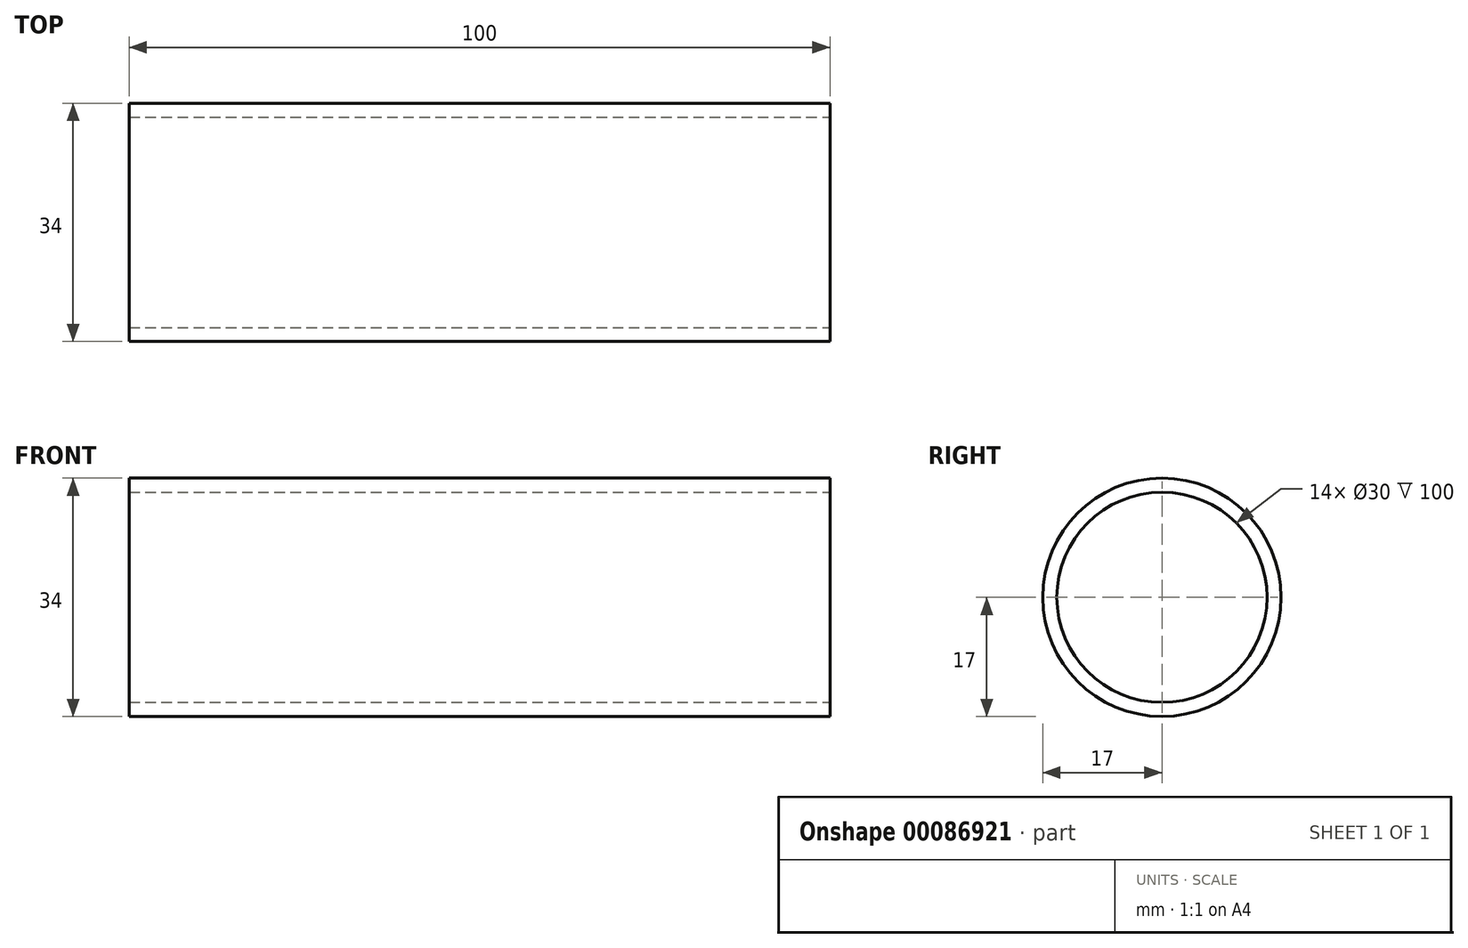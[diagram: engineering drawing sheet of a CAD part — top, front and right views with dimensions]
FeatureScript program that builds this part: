
annotation { "Feature Type Name" : "Feature", "Feature Type Description" : "" }
export const myFeature = defineFeature(function(context is Context, id is Id, definition is map)
    precondition{}
    {
        {
            var Q0;
            Q0=qCreatedBy(makeId("Top.planeOp"),FACE);
            var sketch = newSketch(context, id + "F0", { "sketchPlane" : qUnion([Q0])});
            skLineSegment(sketch, "E0", {"start": v(-50, 17) * mm, "end": v(50, 17) * mm});
            skLineSegment(sketch, "E1", {"start": v(50, 17) * mm, "end": v(50, 15) * mm});
            skLineSegment(sketch, "E2", {"start": v(50, 15) * mm, "end": v(-50, 15) * mm});
            skLineSegment(sketch, "E3", {"start": v(-50, 15) * mm, "end": v(-50, 17) * mm});
            skLineSegment(sketch, "E4", {"start": v(0, 0) * mm, "end": v(-50, 0) * mm, "construction": true});
            skLineSegment(sketch, "E5", {"start": v(-50, 0) * mm, "end": v(-50, 15) * mm, "construction": true});
            skLineSegment(sketch, "E6", {"start": v(0, 0) * mm, "end": v(50, 0) * mm, "construction": true});
            skLineSegment(sketch, "E7", {"start": v(50, 0) * mm, "end": v(50, 15) * mm, "construction": true});
            skSolve(sketch);
        }
        {
            var Q0;
            Q0 = qSketchRegion(id + "F0", true);
            var Q1;
            Q1=sQuery(id+"F0.wireOp",EDGE,"E4");
            revolve(context, id + "F1", {"entities" : qUnion([Q0]), "axis" : qUnion([Q1]), "revolveType" : RevolveType.FULL});
        }
    });
